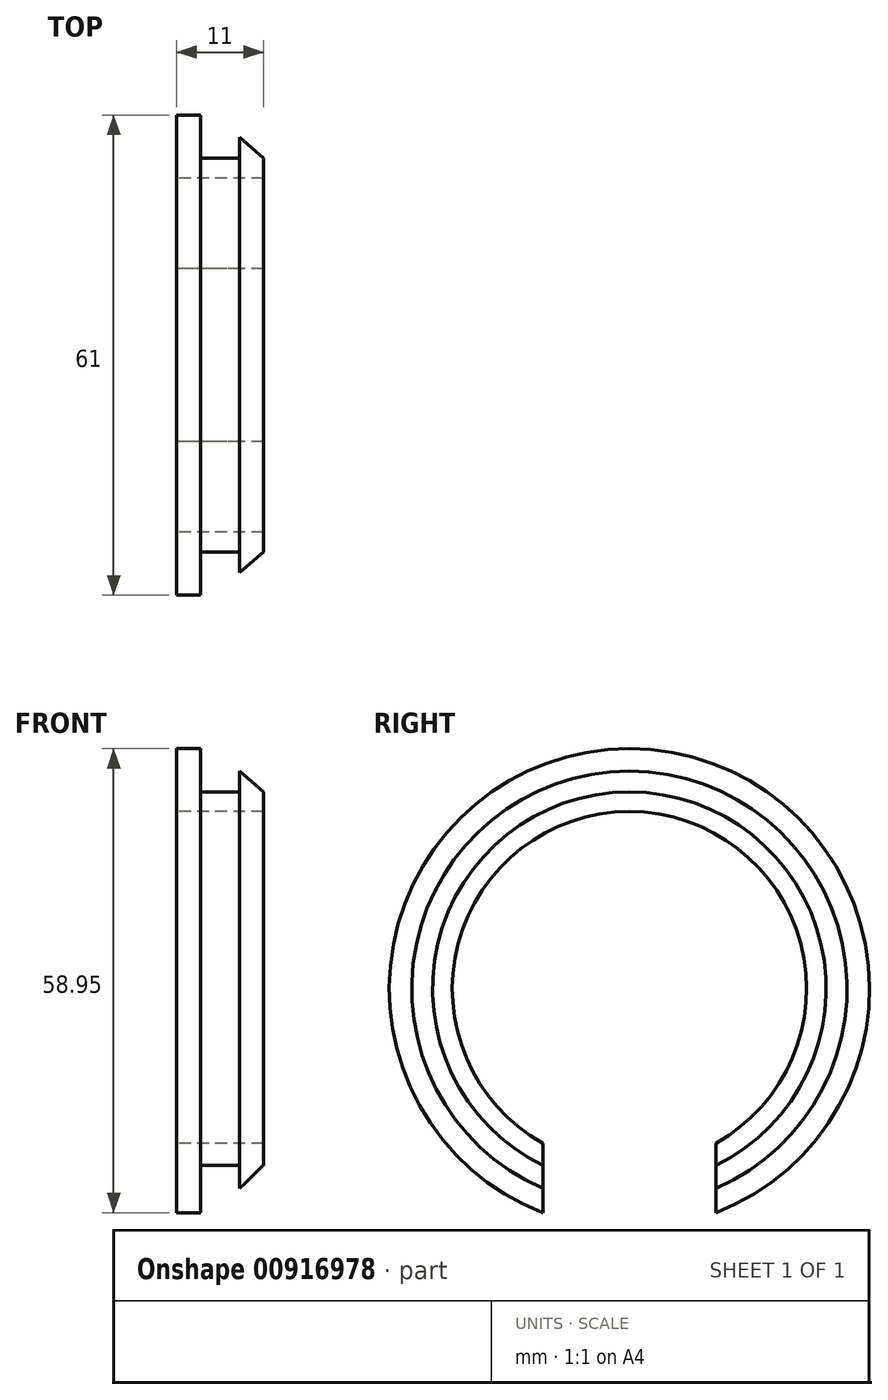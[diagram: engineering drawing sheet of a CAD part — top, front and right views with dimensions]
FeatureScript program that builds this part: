
annotation { "Feature Type Name" : "Feature", "Feature Type Description" : "" }
export const myFeature = defineFeature(function(context is Context, id is Id, definition is map)
    precondition{}
    {
        {
            var Q0;
            Q0=qCreatedBy(makeId("Front.planeOp"),FACE);
            var sketch = newSketch(context, id + "F0", { "sketchPlane" : qUnion([Q0])});
            skLineSegment(sketch, "E0", {"start": v(0, 0) * mm, "end": v(32.61, 0) * mm, "construction": true});
            skLineSegment(sketch, "E1", {"start": v(0, 22.5) * mm, "end": v(11, 22.5) * mm});
            skLineSegment(sketch, "E2", {"start": v(11, 22.5) * mm, "end": v(11, 25) * mm});
            skLineSegment(sketch, "E3", {"start": v(11, 25) * mm, "end": v(8, 27.65) * mm});
            skLineSegment(sketch, "E4", {"start": v(8, 27.65) * mm, "end": v(8, 25) * mm});
            skLineSegment(sketch, "E5", {"start": v(8, 25) * mm, "end": v(3, 25) * mm});
            skLineSegment(sketch, "E6", {"start": v(3, 25) * mm, "end": v(3, 30.5) * mm});
            skLineSegment(sketch, "E7", {"start": v(3, 30.5) * mm, "end": v(0, 30.5) * mm});
            skLineSegment(sketch, "E8", {"start": v(0, 30.5) * mm, "end": v(0, 22.5) * mm});
            skSolve(sketch);
        }
        {
            var Q0;
            Q0=makeQuery(id+"F0.imprint","IMPRINT",FACE,{"disambiguationData":[TD([[makeQuery(id+"F0.imprint","IMPRINT",EDGE,{"derivedFrom":sQuery(id+"F0.wireOp",EDGE,"E1")}),1.0]])]});
            var Q1;
            Q1=sQuery(id+"F0.wireOp",EDGE,"E0");
            revolve(context, id + "F1", {"surfaceOperationType" : NewSurfaceOperationType.NEW, "entities" : qUnion([Q0]), "axis" : qUnion([Q1]), "revolveType" : RevolveType.FULL});
        }
        {
            var Q0;
            Q0=makeQuery(id+"F1.opRevolve","SWEPT_FACE",FACE,{"disambiguationData":[OSD([sQuery(id+"F0.wireOp",EDGE,"E8")])]});
            var sketch = newSketch(context, id + "F2", { "sketchPlane" : qUnion([Q0])});
            skLineSegment(sketch, "E9.0", {"start": v(-11, -19.63) * mm, "end": v(-11, -28.45) * mm});
            skLineSegment(sketch, "E10.0", {"start": v(11, -19.63) * mm, "end": v(11, -28.45) * mm});
            skArc(sketch, "E11", {"start": v(-11, -19.63) * mm, "mid": v(0, -22.5) * mm, "end": v(11, -19.63) * mm});
            skArc(sketch, "E12", {"start": v(-11, -28.45) * mm, "mid": v(0, -30.5) * mm, "end": v(11, -28.45) * mm});
            skSolve(sketch);
        }
        {
            var Q0;
            Q0 = qSketchRegion(id + "F2", true);
            extrude(context, id + "F3", {"entities" : qUnion([Q0]), "operationType" : NewBodyOperationType.REMOVE, "endBound" : BoundingType.THROUGH_ALL, "oppositeDirection" : true, "depth" : 25 * mm, "offsetDistance" : 25 * mm});
        }
    });
